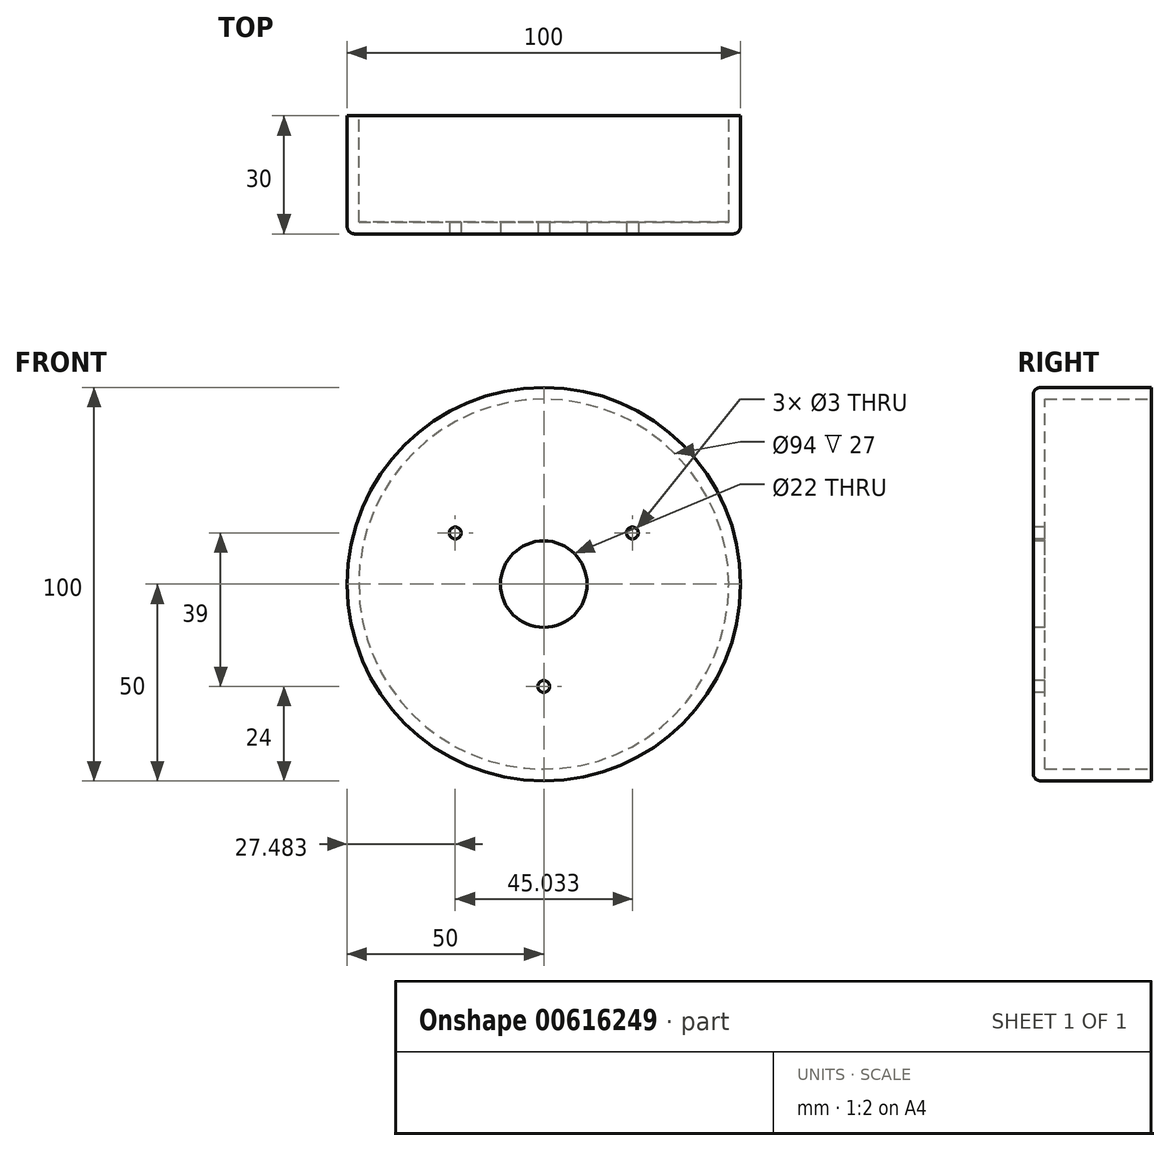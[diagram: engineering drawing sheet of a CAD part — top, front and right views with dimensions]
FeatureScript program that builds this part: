
annotation { "Feature Type Name" : "Feature", "Feature Type Description" : "" }
export const myFeature = defineFeature(function(context is Context, id is Id, definition is map)
    precondition{}
    {
        {
            var Q0;
            Q0=qCreatedBy(makeId("Front.planeOp"),FACE);
            var sketch = newSketch(context, id + "F0", { "sketchPlane" : qUnion([Q0])});
            skCircle(sketch, "E0", {"center": v(0, 0) * mm, "radius": 50 * mm});
            skSolve(sketch);
        }
        {
            var Q0;
            Q0=qSketchRegion(id+"F0",true);
            extrude(context, id + "F1", {"entities" : qUnion([Q0]), "depth" : 30 * mm});
        }
        {
            var Q0;
            Q0=makeQuery(id+"F1.opExtrude","CAP_FACE",FACE,{"disambiguationData":[OSD([sQuery(id+"F0.wireOp",EDGE,"E0")])],"isStart":true});
            shell(context, id + "F2", {"entities" : qUnion([Q0]), "thickness" : 3 * mm});
        }
        {
            var Q0;
            Q0=makeQuery(id+"F1.opExtrude","CAP_EDGE",EDGE,{"disambiguationData":[OSD([sQuery(id+"F0.wireOp",EDGE,"E0")])],"isStart":false});
            fillet(context, id + "F3", {"entities" : qUnion([Q0]), "radius" : 2 * mm, "tangentPropagation" : true, "allowEdgeOverflow" : false});
        }
        {
            var Q0;
            Q0=makeQuery(id+"F1.opExtrude","CAP_FACE",FACE,{"disambiguationData":[OSD([sQuery(id+"F0.wireOp",EDGE,"E0")])],"isStart":false});
            var sketch = newSketch(context, id + "F4", { "sketchPlane" : qUnion([Q0])});
            skPoint(sketch, "E1", {"position": v(0, 0) * mm});
            skSolve(sketch);
        }
        {
            var Q0;
            Q0=sQuery(id+"F4.wireOp",VERTEX,"E1");
            var Q1;
            Q1=makeQuery(id+"F1.opExtrude","SWEPT_BODY",BODY,{"disambiguationData":[OSD([sQuery(id+"F0.wireOp",EDGE,"E0")])]});
            hole(context, id + "F5", {"style" : HoleStyle.SIMPLE, "endStyle" : HoleEndStyle.THROUGH, "holeDiameter" : 22 * mm, "locations" : qUnion([Q0]), "scope" : qUnion([Q1]), "majorDiameter" : 5 * mm, "tappedDepth" : 12 * mm, "tapClearance" : 3});
        }
        {
            var Q0;
            Q0=makeQuery(id+"F1.opExtrude","CAP_FACE",FACE,{"disambiguationData":[OSD([sQuery(id+"F0.wireOp",EDGE,"E0")])],"isStart":false});
            var sketch = newSketch(context, id + "F6", { "sketchPlane" : qUnion([Q0])});
            skPoint(sketch, "E2", {"position": v(0, -26) * mm});
            skPoint(sketch, "E3.1.0", {"position": v(22.52, 13) * mm});
            skPoint(sketch, "E3.2.0", {"position": v(-22.52, 13) * mm});
            skPoint(sketch, "E3.center", {"position": v(0, 0) * mm});
            skSolve(sketch);
        }
        {
            var Q0;
            Q0=sQuery(id+"F6.wireOp",VERTEX,"E2");
            var Q1;
            Q1=sQuery(id+"F6.wireOp",VERTEX,"E3.2.0");
            var Q2;
            Q2=sQuery(id+"F6.wireOp",VERTEX,"E3.1.0");
            var Q3;
            Q3=makeQuery(id+"F1.opExtrude","SWEPT_BODY",BODY,{"disambiguationData":[OSD([sQuery(id+"F0.wireOp",EDGE,"E0")])]});
            hole(context, id + "F7", {"style" : HoleStyle.SIMPLE, "endStyle" : HoleEndStyle.THROUGH, "holeDiameter" : 3 * mm, "majorDiameter" : 5 * mm, "isTappedThrough" : true, "tappedDepth" : 12 * mm, "tapClearance" : 3, "locations" : qUnion([Q0, Q1, Q2]), "scope" : qUnion([Q3])});
        }
    });
